# Revit family: HL_Уличный трап для приема воды из наружных ливнестоков_HL600NHO
name_source: partatom
category: Příslušenství trubek
revit_build: Autodesk Revit 2016 (Build: 20161004_0715(x64)
units: mm (PartAtom-declared; Revit-internal decimal feet)

## family parameters
Kóta kulaté spojky = Použít průměr
Nadpis OmniClass = Liquid Waste Handling Services
Ořezat dutým tvarem při načtení = Ne
Sdílené = Ne
Typ součásti = Normální
Vždy vertikální = Ano
Založené na pracovní rovině = Ne
Číslo OmniClass = 23.70.50.00

## types (1)
- HL600NHO
    Cena = 0 $
    EAN = 9003076045594
    Klíčová poznámka = HL600NHO
    Komentáře k typům = Дождеприёмник с горизонтальным входным патрубком для декоративной облицовки фасадов
    Model = HL600NHO
    Popis = Дождеприёмник с горизонтальным входным патрубком для декоративной облицовки фасадов
    URL = http://www.hutterer-lechner.com
    Výrobce = HL Hutterer & Lechner GmbH
    d = 321 mm
    e = 165 mm
    ВЕС = 1,556 kg
    МАТЕРИАЛ = PP
    НОМИНАЛЬНЫЙ ДИАМЕТР 2 = 110 mm
    ПРИЁМНОЕ ОТВЕРСТИЕ = DN110 waagrecht
    ПРОИЗВОДИТЕЛЬНОСТЬ = DN110: 10 l/s. DN125: 11 l/s
    ПРОПУСКНАЯ СПОСОБНОСТЬ = 0.0 m³/h
    РАЗМЕР = DN110/125
    материал = Plactic - Black
